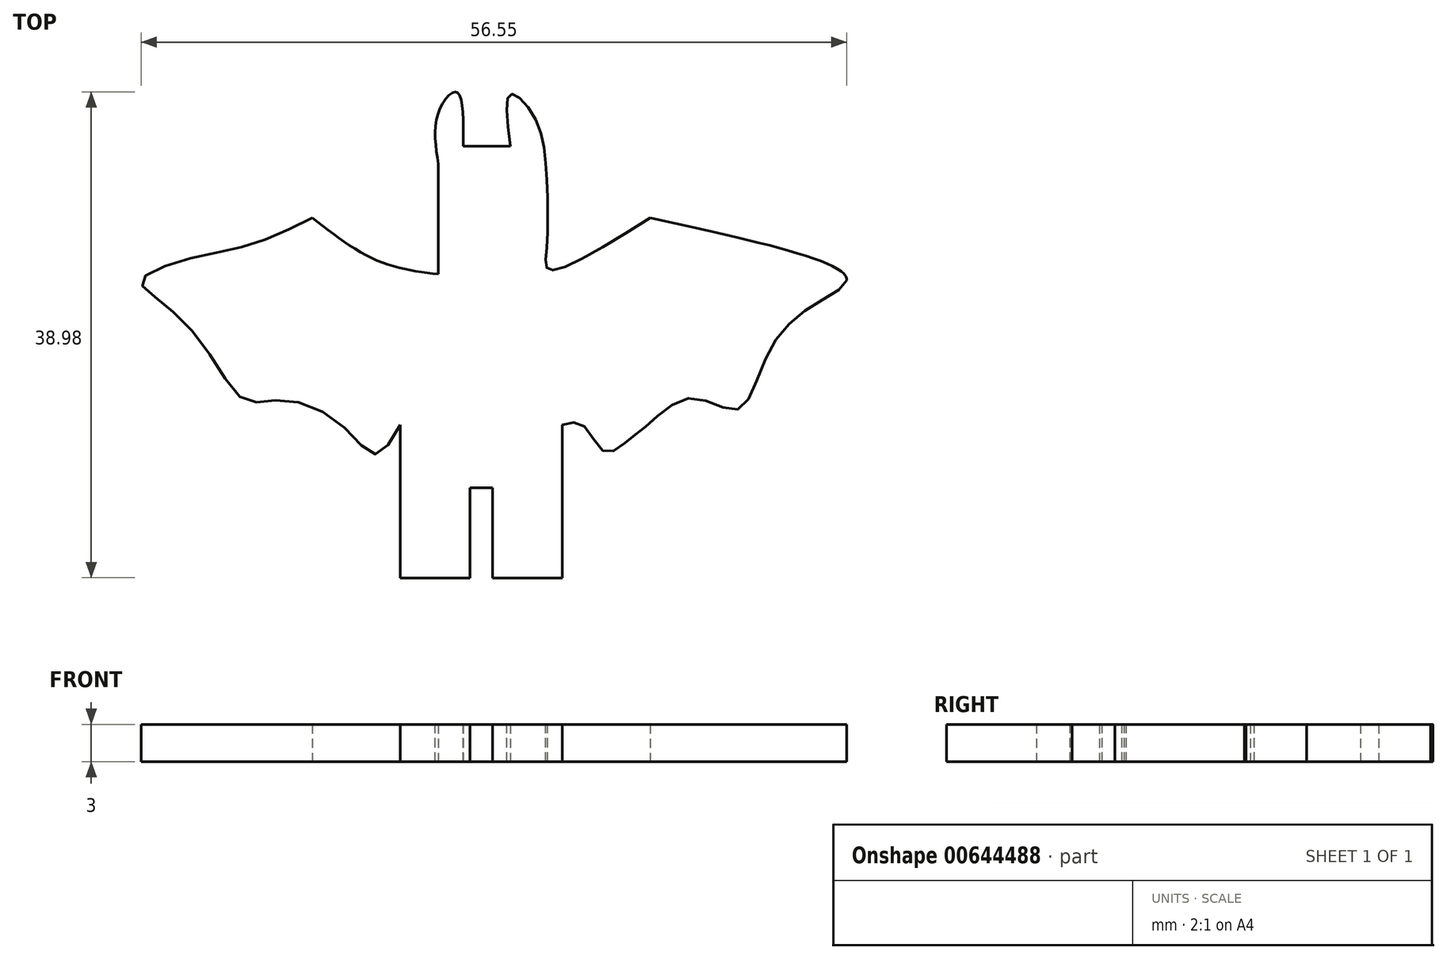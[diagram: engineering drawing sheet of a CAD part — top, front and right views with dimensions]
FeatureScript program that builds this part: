
annotation { "Feature Type Name" : "Feature", "Feature Type Description" : "" }
export const myFeature = defineFeature(function(context is Context, id is Id, definition is map)
    precondition{}
    {
        {
            var Q0;
            Q0=qCreatedBy(makeId("Top.planeOp"),FACE);
            var sketch = newSketch(context, id + "F0", { "sketchPlane" : qUnion([Q0])});
            skLineSegment(sketch, "E0.bottom", {"start": v(0, 0) * mm, "end": v(-80, 0) * mm});
            skLineSegment(sketch, "E0.top", {"start": v(0, 50) * mm, "end": v(-80, 50) * mm});
            skLineSegment(sketch, "E0.left", {"start": v(0, 0) * mm, "end": v(0, 50) * mm});
            skLineSegment(sketch, "E0.right", {"start": v(-80, 0) * mm, "end": v(-80, 50) * mm});
            skFitSpline(sketch, "E1", {"points": [v(-42.82, 31.93) * mm, v(-37.6, 28.5) * mm, v(-32.72, 27.42) * mm], "startDerivative": vector(9.8, -7.6) * mm, "endDerivative": vector(10.42, -1.3) * mm});
            skLineSegment(sketch, "E2", {"start": v(-32.72, 27.42) * mm, "end": v(-32.72, 36.26) * mm});
            skFitSpline(sketch, "E3", {"points": [v(-32.72, 36.26) * mm, v(-32.72, 40.41) * mm, v(-31.28, 42.04) * mm, v(-30.73, 37.7) * mm], "startDerivative": vector(-1.92, 11.88) * mm, "endDerivative": vector(-0.14, -16.72) * mm});
            skLineSegment(sketch, "E4", {"start": v(-30.73, 37.7) * mm, "end": v(-26.95, 37.7) * mm});
            skFitSpline(sketch, "E5", {"points": [v(-26.95, 37.7) * mm, v(-26.95, 41.86) * mm, v(-25.14, 40.23) * mm, v(-24.06, 35.54) * mm, v(-24.06, 29.4) * mm, v(-23.88, 27.78) * mm, v(-15.76, 31.93) * mm], "startDerivative": vector(-4.8, 36.33) * mm, "endDerivative": vector(45.17, 28.2) * mm});
            skPoint(sketch, "E6.2.internal.snap0", {"position": v(0, 25) * mm});
            skFitSpline(sketch, "E6", {"points": [v(-15.76, 31.93) * mm, v(0, 27.06) * mm, v(-2.6, 25) * mm, v(-6.38, 20.93) * mm, v(-8.72, 16.6) * mm, v(-12.33, 17.5) * mm, v(-15.76, 15.52) * mm, v(-17.56, 14.07) * mm, v(-19.38, 13.17) * mm, v(-21.17, 15.34) * mm, v(-22.8, 15.34) * mm], "startDerivative": vector(116.51, -25.32) * mm, "endDerivative": vector(-27.15, -8.73) * mm});
            skLineSegment(sketch, "E7", {"start": v(-22.8, 15.34) * mm, "end": v(-22.8, 3.07) * mm});
            skLineSegment(sketch, "E8", {"start": v(-22.8, 3.07) * mm, "end": v(-28.39, 3.07) * mm});
            skLineSegment(sketch, "E9", {"start": v(-28.39, 3.07) * mm, "end": v(-28.39, 10.28) * mm});
            skLineSegment(sketch, "E10", {"start": v(-28.39, 10.28) * mm, "end": v(-30.2, 10.28) * mm});
            skLineSegment(sketch, "E11", {"start": v(-30.2, 10.28) * mm, "end": v(-30.2, 4.7) * mm});
            skLineSegment(sketch, "E12", {"start": v(-30.2, 4.7) * mm, "end": v(-30.2, 3.07) * mm});
            skLineSegment(sketch, "E13", {"start": v(-30.2, 3.07) * mm, "end": v(-35.79, 3.07) * mm});
            skLineSegment(sketch, "E14", {"start": v(-35.79, 3.07) * mm, "end": v(-35.79, 15.34) * mm});
            skFitSpline(sketch, "E15", {"points": [v(-35.79, 15.34) * mm, v(-37.77, 12.99) * mm, v(-40.48, 15.34) * mm, v(-45.35, 17.32) * mm, v(-48.23, 17.32) * mm, v(-51.48, 21.65) * mm, v(-55.45, 25.62) * mm, v(-56.53, 26.88) * mm, v(-53.29, 28.5) * mm, v(-47.87, 29.77) * mm, v(-42.82, 31.93) * mm], "startDerivative": vector(-22.37, -40.44) * mm, "endDerivative": vector(43.05, 21.3) * mm});
            skCircle(sketch, "E16", {"center": v(-41.4, 24.72) * mm, "radius": 3.08 * mm});
            skSolve(sketch);
        }
        {
            var Q0;
            Q0=makeQuery(id+"F0.imprint","IMPRINT",FACE,{"disambiguationData":[TD([[makeQuery(id+"F0.imprint","IMPRINT",EDGE,{"derivedFrom":sQuery(id+"F0.wireOp",EDGE,"E1")}),-1.0]])]});
            var Q1;
            Q1=makeQuery(id+"F0.imprint","IMPRINT",FACE,{"disambiguationData":[TD([[makeQuery(id+"F0.imprint","IMPRINT",EDGE,{"derivedFrom":sQuery(id+"F0.wireOp",EDGE,"E16")}),1.0]])]});
            extrude(context, id + "F1", {"entities" : qUnion([Q0, Q1]), "depth" : 3 * mm, "offsetDistance" : 25 * mm});
        }
    });
